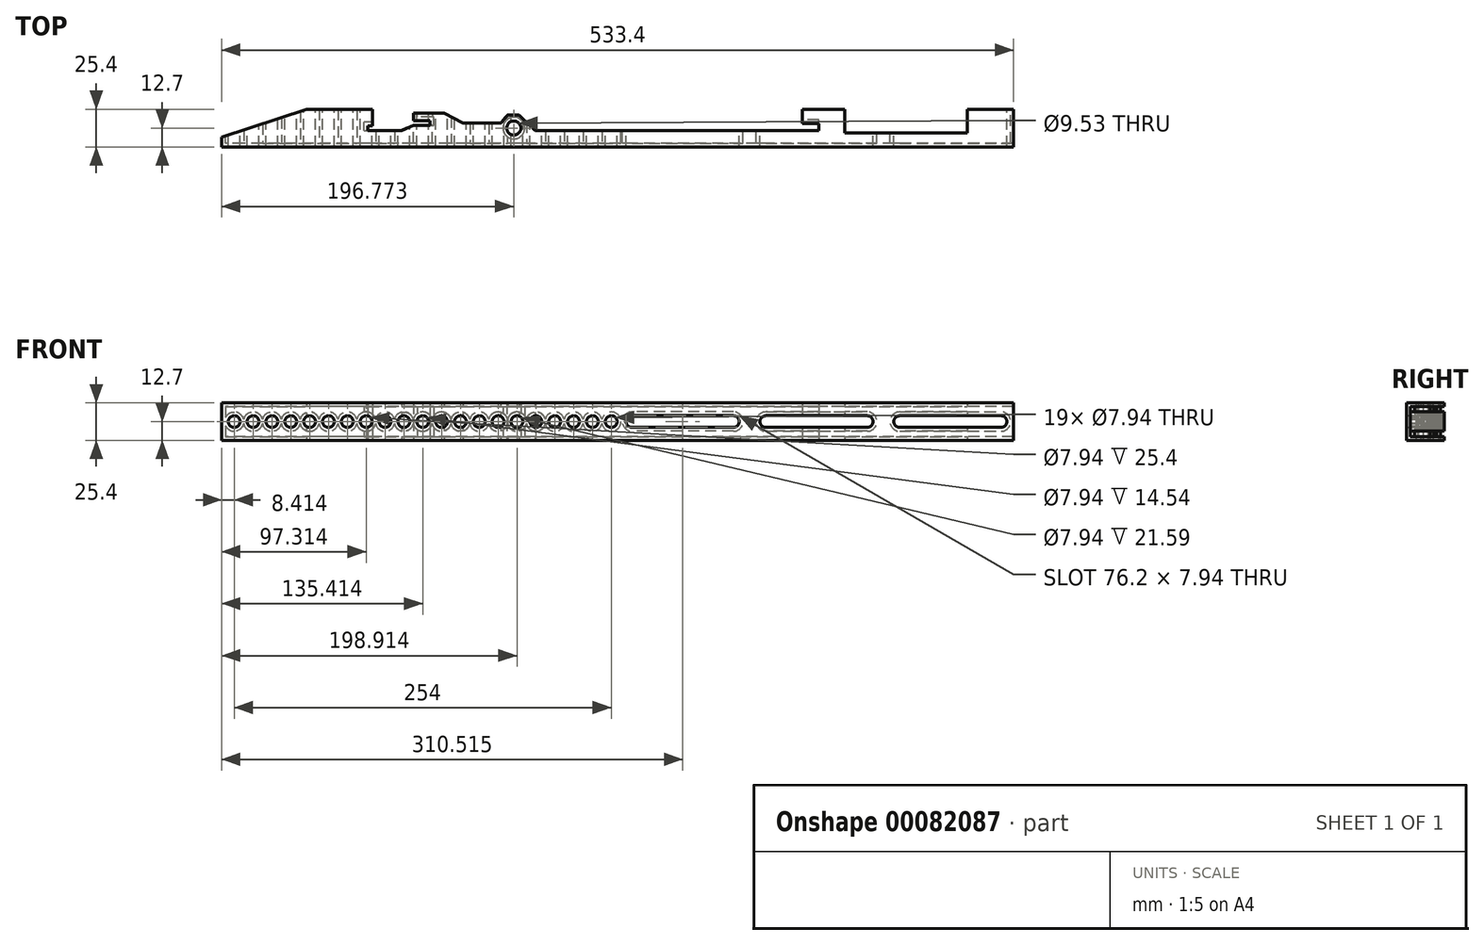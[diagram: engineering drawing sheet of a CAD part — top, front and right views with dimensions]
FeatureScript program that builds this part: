
annotation { "Feature Type Name" : "Feature", "Feature Type Description" : "" }
export const myFeature = defineFeature(function(context is Context, id is Id, definition is map)
    precondition{}
    {
        {
            var Q0;
            Q0=qCreatedBy(makeId("Front.planeOp"),FACE);
            var sketch = newSketch(context, id + "F0", { "sketchPlane" : qUnion([Q0])});
            skLineSegment(sketch, "E0.bottom", {"start": v(0, 0) * mm, "end": v(-533.4, 0) * mm});
            skLineSegment(sketch, "E0.top", {"start": v(0, 25.4) * mm, "end": v(-533.4, 25.4) * mm});
            skLineSegment(sketch, "E0.left", {"start": v(0, 0) * mm, "end": v(0, 25.4) * mm});
            skLineSegment(sketch, "E0.right", {"start": v(-533.4, 0) * mm, "end": v(-533.4, 25.4) * mm});
            skLineSegment(sketch, "E1", {"start": v(-266.7, 25.4) * mm, "end": v(-266.7, 0) * mm, "construction": true});
            skLineSegment(sketch, "E2", {"start": v(0, 12.7) * mm, "end": v(-533.4, 12.7) * mm, "construction": true});
            skCircle(sketch, "E3", {"center": v(-524.99, 12.7) * mm, "radius": 3.97 * mm});
            skCircle(sketch, "E4.1.0.0", {"center": v(-512.29, 12.7) * mm, "radius": 3.97 * mm});
            skCircle(sketch, "E4.2.0.0", {"center": v(-499.59, 12.7) * mm, "radius": 3.97 * mm});
            skCircle(sketch, "E4.3.0.0", {"center": v(-486.89, 12.7) * mm, "radius": 3.97 * mm});
            skCircle(sketch, "E4.4.0.0", {"center": v(-474.19, 12.7) * mm, "radius": 3.97 * mm});
            skCircle(sketch, "E4.5.0.0", {"center": v(-461.49, 12.7) * mm, "radius": 3.97 * mm});
            skCircle(sketch, "E4.6.0.0", {"center": v(-448.79, 12.7) * mm, "radius": 3.97 * mm});
            skCircle(sketch, "E4.7.0.0", {"center": v(-436.09, 12.7) * mm, "radius": 3.97 * mm});
            skCircle(sketch, "E4.8.0.0", {"center": v(-423.39, 12.7) * mm, "radius": 3.97 * mm});
            skCircle(sketch, "E4.9.0.0", {"center": v(-410.69, 12.7) * mm, "radius": 3.97 * mm});
            skCircle(sketch, "E4.10.0.0", {"center": v(-397.99, 12.7) * mm, "radius": 3.97 * mm});
            skCircle(sketch, "E4.11.0.0", {"center": v(-385.29, 12.7) * mm, "radius": 3.97 * mm});
            skCircle(sketch, "E4.12.0.0", {"center": v(-372.59, 12.7) * mm, "radius": 3.97 * mm});
            skCircle(sketch, "E4.13.0.0", {"center": v(-359.89, 12.7) * mm, "radius": 3.97 * mm});
            skCircle(sketch, "E4.14.0.0", {"center": v(-347.19, 12.7) * mm, "radius": 3.97 * mm});
            skCircle(sketch, "E4.15.0.0", {"center": v(-334.49, 12.7) * mm, "radius": 3.97 * mm});
            skCircle(sketch, "E4.16.0.0", {"center": v(-321.79, 12.7) * mm, "radius": 3.97 * mm});
            skCircle(sketch, "E4.17.0.0", {"center": v(-309.09, 12.7) * mm, "radius": 3.97 * mm});
            skCircle(sketch, "E4.18.0.0", {"center": v(-296.39, 12.7) * mm, "radius": 3.97 * mm});
            skCircle(sketch, "E4.19.0.0", {"center": v(-283.69, 12.7) * mm, "radius": 3.97 * mm});
            skCircle(sketch, "E4.20.0.0", {"center": v(-270.99, 12.7) * mm, "radius": 3.97 * mm});
            skLineSegment(sketch, "E4.direction1", {"start": v(-524.99, 12.7) * mm, "end": v(-512.29, 12.7) * mm, "construction": true});
            skCircle(sketch, "E5", {"center": v(-8.41, 12.7) * mm, "radius": 3.97 * mm});
            skCircle(sketch, "E6", {"center": v(-76.68, 12.7) * mm, "radius": 3.97 * mm});
            skLineSegment(sketch, "E7", {"start": v(-76.68, 16.67) * mm, "end": v(-8.41, 16.67) * mm});
            skLineSegment(sketch, "E8", {"start": v(-76.68, 8.73) * mm, "end": v(-8.41, 8.73) * mm});
            skCircle(sketch, "E9.1.0.0", {"center": v(-98.58, 12.7) * mm, "radius": 3.97 * mm});
            skLineSegment(sketch, "E9.1.0.1", {"start": v(-166.85, 8.73) * mm, "end": v(-98.58, 8.73) * mm});
            skLineSegment(sketch, "E9.1.0.2", {"start": v(-166.85, 16.67) * mm, "end": v(-98.58, 16.67) * mm});
            skCircle(sketch, "E9.1.0.3", {"center": v(-166.85, 12.7) * mm, "radius": 3.97 * mm});
            skCircle(sketch, "E9.2.0.0", {"center": v(-188.75, 12.7) * mm, "radius": 3.97 * mm});
            skLineSegment(sketch, "E9.2.0.1", {"start": v(-257.02, 8.73) * mm, "end": v(-188.75, 8.73) * mm});
            skLineSegment(sketch, "E9.2.0.2", {"start": v(-257.02, 16.67) * mm, "end": v(-188.75, 16.67) * mm});
            skCircle(sketch, "E9.2.0.3", {"center": v(-257.02, 12.7) * mm, "radius": 3.97 * mm});
            skLineSegment(sketch, "E9.direction1", {"start": v(-8.41, 12.7) * mm, "end": v(-98.58, 12.7) * mm, "construction": true});
            skSolve(sketch);
        }
        {
            var Q0;
            Q0=makeQuery(id+"F0.imprint","IMPRINT",FACE,{"disambiguationData":[TD([[makeQuery(id+"F0.imprint","IMPRINT",EDGE,{"derivedFrom":sQuery(id+"F0.wireOp",EDGE,"E0.bottom")}),-1.0]])]});
            extrude(context, id + "F1", {"entities" : qUnion([Q0]), "depth" : 25.4 * mm});
        }
        {
            var Q0;
            Q0=makeQuery(id+"F1.opExtrude","SWEPT_FACE",FACE,{"disambiguationData":[OSD([sQuery(id+"F0.wireOp",EDGE,"E0.bottom")])]});
            var sketch = newSketch(context, id + "F2", { "sketchPlane" : qUnion([Q0])});
            skLineSegment(sketch, "E10.0", {"start": v(0, 25.4) * mm, "end": v(-533.4, 25.4) * mm});
            skLineSegment(sketch, "E10.1", {"start": v(-533.4, 25.4) * mm, "end": v(-533.4, 0) * mm});
            skLineSegment(sketch, "E10.2", {"start": v(0, 0) * mm, "end": v(-533.4, 0) * mm});
            skLineSegment(sketch, "E10.3", {"start": v(0, 25.4) * mm, "end": v(0, 0) * mm});
            skLineSegment(sketch, "E11", {"start": v(-533.4, 18.84) * mm, "end": v(-476.25, 0) * mm});
            skLineSegment(sketch, "E12", {"start": v(-476.25, 0) * mm, "end": v(-431.8, 0) * mm});
            skLineSegment(sketch, "E13", {"start": v(-431.8, 0) * mm, "end": v(-431.8, 11.11) * mm});
            skLineSegment(sketch, "E14", {"start": v(-431.8, 11.11) * mm, "end": v(-434.98, 11.11) * mm});
            skLineSegment(sketch, "E15", {"start": v(-434.98, 11.11) * mm, "end": v(-434.98, 14.29) * mm});
            skLineSegment(sketch, "E16", {"start": v(-434.98, 14.29) * mm, "end": v(-412.11, 14.29) * mm});
            skLineSegment(sketch, "E17", {"start": v(-412.11, 14.29) * mm, "end": v(-404.17, 10.86) * mm});
            skLineSegment(sketch, "E18", {"start": v(-404.17, 10.86) * mm, "end": v(-393.06, 10.86) * mm});
            skLineSegment(sketch, "E19", {"start": v(-393.06, 10.86) * mm, "end": v(-393.06, 7.68) * mm});
            skLineSegment(sketch, "E20", {"start": v(-393.06, 7.68) * mm, "end": v(-404.17, 7.68) * mm});
            skLineSegment(sketch, "E21", {"start": v(-404.17, 7.68) * mm, "end": v(-404.17, 2.55) * mm});
            skLineSegment(sketch, "E22", {"start": v(-404.17, 2.55) * mm, "end": v(-383.54, 2.55) * mm});
            skLineSegment(sketch, "E23", {"start": v(-383.54, 2.55) * mm, "end": v(-370.84, 9.38) * mm});
            skLineSegment(sketch, "E24", {"start": v(-370.84, 9.38) * mm, "end": v(-345.44, 9.38) * mm});
            skLineSegment(sketch, "E25", {"start": v(-345.44, 9.38) * mm, "end": v(-340.79, 3.8) * mm});
            skLineSegment(sketch, "E26", {"start": v(-340.79, 3.8) * mm, "end": v(-333, 3.8) * mm});
            skLineSegment(sketch, "E27", {"start": v(-333, 3.8) * mm, "end": v(-322.3, 14.29) * mm});
            skLineSegment(sketch, "E28", {"start": v(-322.3, 14.29) * mm, "end": v(-131.13, 14.29) * mm});
            skLineSegment(sketch, "E29", {"start": v(-131.13, 14.29) * mm, "end": v(-131.13, 9.52) * mm});
            skLineSegment(sketch, "E30", {"start": v(-131.13, 9.52) * mm, "end": v(-142.24, 9.52) * mm});
            skLineSegment(sketch, "E31", {"start": v(-142.24, 9.52) * mm, "end": v(-142.24, 0) * mm});
            skLineSegment(sketch, "E32", {"start": v(-142.24, 0) * mm, "end": v(-113.67, 0) * mm});
            skLineSegment(sketch, "E33", {"start": v(-113.67, 0) * mm, "end": v(-113.67, 15.87) * mm});
            skLineSegment(sketch, "E34", {"start": v(-113.67, 15.87) * mm, "end": v(-31.12, 15.88) * mm});
            skLineSegment(sketch, "E35", {"start": v(-31.12, 15.88) * mm, "end": v(-31.12, 0) * mm});
            skLineSegment(sketch, "E36", {"start": v(-533.4, 12.7) * mm, "end": v(0, 12.7) * mm, "construction": true});
            skCircle(sketch, "E37", {"center": v(-336.63, 12.7) * mm, "radius": 4.76 * mm});
            skSolve(sketch);
        }
        {
            var Q0;
            {var subQ0=sQuery(id+"F2.wireOp",EDGE,"E13");Q0=makeQuery(id+"F2.imprint","IMPRINT",FACE,{"disambiguationData":[TD([[makeQuery(id+"F2.imprint","IMPRINT",EDGE,{"derivedFrom":subQ0}),-1.0]])]});}
            var Q1;
            Q1=makeQuery(id+"F2.imprint","IMPRINT",FACE,{"disambiguationData":[TD([[makeQuery(id+"F2.imprint","IMPRINT",EDGE,{"derivedFrom":sQuery(id+"F2.wireOp",EDGE,"E37")}),1.0]])]});
            var Q2;
            {var subQ3=sQuery(id+"F2.wireOp",EDGE,"E11");Q2=makeQuery(id+"F2.imprint","IMPRINT",FACE,{"disambiguationData":[TD([[makeQuery(id+"F2.imprint","IMPRINT",EDGE,{"derivedFrom":subQ3}),-1.0]])]});}
            var Q3;
            {var subQ0=sQuery(id+"F2.wireOp",EDGE,"E33");Q3=makeQuery(id+"F2.imprint","IMPRINT",FACE,{"disambiguationData":[TD([[makeQuery(id+"F2.imprint","IMPRINT",EDGE,{"derivedFrom":subQ0}),-1.0]])]});}
            extrude(context, id + "F3", {"entities" : qUnion([Q0, Q1, Q2, Q3]), "operationType" : NewBodyOperationType.REMOVE, "endBound" : BoundingType.THROUGH_ALL, "oppositeDirection" : true, "depth" : 25.4 * mm});
        }
        {
            var Q0;
            Q0=makeQuery(id+"F3.boolean.opBoolean","COPY",FACE,{"derivedFrom":makeQuery(id+"F3.opExtrude","SWEPT_FACE",FACE,{"disambiguationData":[OSD([sQuery(id+"F2.wireOp",EDGE,"E11")])]})});
            var Q1;
            {var subQ0=sQuery(id+"F0.wireOp",EDGE,"E4.5.0.0");var subQ1=sQuery(id+"F0.wireOp",EDGE,"E4.4.0.0");var subQ2=sQuery(id+"F0.wireOp",EDGE,"E0.top");var subQ3=sQuery(id+"F0.wireOp",EDGE,"E0.bottom");var subQ4=sQuery(id+"F0.wireOp",EDGE,"E4.6.0.0");var subQ5=sQuery(id+"F0.wireOp",EDGE,"E4.7.0.0");Q1=makeQuery(id+"F3.boolean.opBoolean","SPLIT",FACE,{"disambiguationData":[TD([makeQuery(id+"F1.opExtrude","SWEPT_FACE",FACE,{"disambiguationData":[OSD([subQ1])]})])],"derivedFrom":makeQuery(id+"F1.opExtrude","CAP_FACE",FACE,{"disambiguationData":[OSD([subQ3,subQ2,sQuery(id+"F0.wireOp",EDGE,"E0.left"),sQuery(id+"F0.wireOp",EDGE,"E0.right"),sQuery(id+"F0.wireOp",EDGE,"E3"),sQuery(id+"F0.wireOp",EDGE,"E4.1.0.0"),sQuery(id+"F0.wireOp",EDGE,"E4.2.0.0"),sQuery(id+"F0.wireOp",EDGE,"E4.3.0.0"),subQ1,subQ0,subQ4,subQ5,sQuery(id+"F0.wireOp",EDGE,"E4.8.0.0"),sQuery(id+"F0.wireOp",EDGE,"E4.9.0.0"),sQuery(id+"F0.wireOp",EDGE,"E4.10.0.0"),sQuery(id+"F0.wireOp",EDGE,"E4.11.0.0"),sQuery(id+"F0.wireOp",EDGE,"E4.12.0.0"),sQuery(id+"F0.wireOp",EDGE,"E4.13.0.0"),sQuery(id+"F0.wireOp",EDGE,"E4.14.0.0"),sQuery(id+"F0.wireOp",EDGE,"E4.15.0.0"),sQuery(id+"F0.wireOp",EDGE,"E4.16.0.0"),sQuery(id+"F0.wireOp",EDGE,"E4.17.0.0"),sQuery(id+"F0.wireOp",EDGE,"E4.18.0.0"),sQuery(id+"F0.wireOp",EDGE,"E4.19.0.0"),sQuery(id+"F0.wireOp",EDGE,"E4.20.0.0"),sQuery(id+"F0.wireOp",EDGE,"E5"),sQuery(id+"F0.wireOp",EDGE,"E6"),sQuery(id+"F0.wireOp",EDGE,"E7"),sQuery(id+"F0.wireOp",EDGE,"E8"),sQuery(id+"F0.wireOp",EDGE,"E9.1.0.0"),sQuery(id+"F0.wireOp",EDGE,"E9.1.0.1"),sQuery(id+"F0.wireOp",EDGE,"E9.1.0.2"),sQuery(id+"F0.wireOp",EDGE,"E9.1.0.3"),sQuery(id+"F0.wireOp",EDGE,"E9.2.0.0"),sQuery(id+"F0.wireOp",EDGE,"E9.2.0.1"),sQuery(id+"F0.wireOp",EDGE,"E9.2.0.2"),sQuery(id+"F0.wireOp",EDGE,"E9.2.0.3")])],"isStart":true})});}
            var Q2;
            Q2=makeQuery(id+"F3.boolean.opBoolean","COPY",FACE,{"derivedFrom":makeQuery(id+"F3.opExtrude","SWEPT_FACE",FACE,{"disambiguationData":[OSD([sQuery(id+"F2.wireOp",EDGE,"E16")])]})});
            var Q3;
            Q3=makeQuery(id+"F3.boolean.opBoolean","COPY",FACE,{"derivedFrom":makeQuery(id+"F3.opExtrude","SWEPT_FACE",FACE,{"disambiguationData":[OSD([sQuery(id+"F2.wireOp",EDGE,"E17")])]})});
            var Q4;
            Q4=makeQuery(id+"F3.boolean.opBoolean","COPY",FACE,{"derivedFrom":makeQuery(id+"F3.opExtrude","SWEPT_FACE",FACE,{"disambiguationData":[OSD([sQuery(id+"F2.wireOp",EDGE,"E22")])]})});
            var Q5;
            Q5=makeQuery(id+"F3.boolean.opBoolean","COPY",FACE,{"derivedFrom":makeQuery(id+"F3.opExtrude","SWEPT_FACE",FACE,{"disambiguationData":[OSD([sQuery(id+"F2.wireOp",EDGE,"E23")])]})});
            var Q6;
            Q6=makeQuery(id+"F3.boolean.opBoolean","COPY",FACE,{"derivedFrom":makeQuery(id+"F3.opExtrude","SWEPT_FACE",FACE,{"disambiguationData":[OSD([sQuery(id+"F2.wireOp",EDGE,"E24")])]})});
            var Q7;
            Q7=makeQuery(id+"F3.boolean.opBoolean","COPY",FACE,{"derivedFrom":makeQuery(id+"F3.opExtrude","SWEPT_FACE",FACE,{"disambiguationData":[OSD([sQuery(id+"F2.wireOp",EDGE,"E26")])]})});
            var Q8;
            Q8=makeQuery(id+"F3.boolean.opBoolean","COPY",FACE,{"derivedFrom":makeQuery(id+"F3.opExtrude","SWEPT_FACE",FACE,{"disambiguationData":[OSD([sQuery(id+"F2.wireOp",EDGE,"E27")])]})});
            var Q9;
            Q9=makeQuery(id+"F3.boolean.opBoolean","COPY",FACE,{"derivedFrom":makeQuery(id+"F3.opExtrude","SWEPT_FACE",FACE,{"disambiguationData":[OSD([sQuery(id+"F2.wireOp",EDGE,"E28")])]})});
            var Q10;
            Q10=makeQuery(id+"F3.boolean.opBoolean","COPY",FACE,{"derivedFrom":makeQuery(id+"F3.opExtrude","SWEPT_FACE",FACE,{"disambiguationData":[OSD([sQuery(id+"F2.wireOp",EDGE,"E34")])]})});
            var Q11;
            {var subQ0=sQuery(id+"F0.wireOp",EDGE,"E0.bottom");var subQ1=sQuery(id+"F0.wireOp",EDGE,"E9.1.0.1");Q11=makeQuery(id+"F3.boolean.opBoolean","SPLIT",FACE,{"disambiguationData":[TD([makeQuery(id+"F1.opExtrude","SWEPT_FACE",FACE,{"disambiguationData":[OSD([subQ1])]})])],"derivedFrom":makeQuery(id+"F1.opExtrude","CAP_FACE",FACE,{"disambiguationData":[OSD([subQ0,sQuery(id+"F0.wireOp",EDGE,"E0.top"),sQuery(id+"F0.wireOp",EDGE,"E0.left"),sQuery(id+"F0.wireOp",EDGE,"E0.right"),sQuery(id+"F0.wireOp",EDGE,"E3"),sQuery(id+"F0.wireOp",EDGE,"E4.1.0.0"),sQuery(id+"F0.wireOp",EDGE,"E4.2.0.0"),sQuery(id+"F0.wireOp",EDGE,"E4.3.0.0"),sQuery(id+"F0.wireOp",EDGE,"E4.4.0.0"),sQuery(id+"F0.wireOp",EDGE,"E4.5.0.0"),sQuery(id+"F0.wireOp",EDGE,"E4.6.0.0"),sQuery(id+"F0.wireOp",EDGE,"E4.7.0.0"),sQuery(id+"F0.wireOp",EDGE,"E4.8.0.0"),sQuery(id+"F0.wireOp",EDGE,"E4.9.0.0"),sQuery(id+"F0.wireOp",EDGE,"E4.10.0.0"),sQuery(id+"F0.wireOp",EDGE,"E4.11.0.0"),sQuery(id+"F0.wireOp",EDGE,"E4.12.0.0"),sQuery(id+"F0.wireOp",EDGE,"E4.13.0.0"),sQuery(id+"F0.wireOp",EDGE,"E4.14.0.0"),sQuery(id+"F0.wireOp",EDGE,"E4.15.0.0"),sQuery(id+"F0.wireOp",EDGE,"E4.16.0.0"),sQuery(id+"F0.wireOp",EDGE,"E4.17.0.0"),sQuery(id+"F0.wireOp",EDGE,"E4.18.0.0"),sQuery(id+"F0.wireOp",EDGE,"E4.19.0.0"),sQuery(id+"F0.wireOp",EDGE,"E4.20.0.0"),sQuery(id+"F0.wireOp",EDGE,"E5"),sQuery(id+"F0.wireOp",EDGE,"E6"),sQuery(id+"F0.wireOp",EDGE,"E7"),sQuery(id+"F0.wireOp",EDGE,"E8"),sQuery(id+"F0.wireOp",EDGE,"E9.1.0.0"),subQ1,sQuery(id+"F0.wireOp",EDGE,"E9.1.0.2"),sQuery(id+"F0.wireOp",EDGE,"E9.1.0.3"),sQuery(id+"F0.wireOp",EDGE,"E9.2.0.0"),sQuery(id+"F0.wireOp",EDGE,"E9.2.0.1"),sQuery(id+"F0.wireOp",EDGE,"E9.2.0.2"),sQuery(id+"F0.wireOp",EDGE,"E9.2.0.3")])],"isStart":true})});}
            var Q12;
            {var subQ0=sQuery(id+"F0.wireOp",EDGE,"E0.top");var subQ1=sQuery(id+"F0.wireOp",EDGE,"E9.1.0.2");Q12=makeQuery(id+"F3.boolean.opBoolean","SPLIT",FACE,{"disambiguationData":[TD([makeQuery(id+"F1.opExtrude","SWEPT_FACE",FACE,{"disambiguationData":[OSD([subQ1])]})])],"derivedFrom":makeQuery(id+"F1.opExtrude","CAP_FACE",FACE,{"disambiguationData":[OSD([sQuery(id+"F0.wireOp",EDGE,"E0.bottom"),subQ0,sQuery(id+"F0.wireOp",EDGE,"E0.left"),sQuery(id+"F0.wireOp",EDGE,"E0.right"),sQuery(id+"F0.wireOp",EDGE,"E3"),sQuery(id+"F0.wireOp",EDGE,"E4.1.0.0"),sQuery(id+"F0.wireOp",EDGE,"E4.2.0.0"),sQuery(id+"F0.wireOp",EDGE,"E4.3.0.0"),sQuery(id+"F0.wireOp",EDGE,"E4.4.0.0"),sQuery(id+"F0.wireOp",EDGE,"E4.5.0.0"),sQuery(id+"F0.wireOp",EDGE,"E4.6.0.0"),sQuery(id+"F0.wireOp",EDGE,"E4.7.0.0"),sQuery(id+"F0.wireOp",EDGE,"E4.8.0.0"),sQuery(id+"F0.wireOp",EDGE,"E4.9.0.0"),sQuery(id+"F0.wireOp",EDGE,"E4.10.0.0"),sQuery(id+"F0.wireOp",EDGE,"E4.11.0.0"),sQuery(id+"F0.wireOp",EDGE,"E4.12.0.0"),sQuery(id+"F0.wireOp",EDGE,"E4.13.0.0"),sQuery(id+"F0.wireOp",EDGE,"E4.14.0.0"),sQuery(id+"F0.wireOp",EDGE,"E4.15.0.0"),sQuery(id+"F0.wireOp",EDGE,"E4.16.0.0"),sQuery(id+"F0.wireOp",EDGE,"E4.17.0.0"),sQuery(id+"F0.wireOp",EDGE,"E4.18.0.0"),sQuery(id+"F0.wireOp",EDGE,"E4.19.0.0"),sQuery(id+"F0.wireOp",EDGE,"E4.20.0.0"),sQuery(id+"F0.wireOp",EDGE,"E5"),sQuery(id+"F0.wireOp",EDGE,"E6"),sQuery(id+"F0.wireOp",EDGE,"E7"),sQuery(id+"F0.wireOp",EDGE,"E8"),sQuery(id+"F0.wireOp",EDGE,"E9.1.0.0"),sQuery(id+"F0.wireOp",EDGE,"E9.1.0.1"),subQ1,sQuery(id+"F0.wireOp",EDGE,"E9.1.0.3"),sQuery(id+"F0.wireOp",EDGE,"E9.2.0.0"),sQuery(id+"F0.wireOp",EDGE,"E9.2.0.1"),sQuery(id+"F0.wireOp",EDGE,"E9.2.0.2"),sQuery(id+"F0.wireOp",EDGE,"E9.2.0.3")])],"isStart":true})});}
            var Q13;
            Q13=makeQuery(id+"F3.boolean.opBoolean","COPY",FACE,{"derivedFrom":makeQuery(id+"F3.opExtrude","SWEPT_FACE",FACE,{"disambiguationData":[OSD([sQuery(id+"F2.wireOp",EDGE,"E13")])]})});
            var Q14;
            Q14=makeQuery(id+"F3.boolean.opBoolean","COPY",FACE,{"derivedFrom":makeQuery(id+"F3.opExtrude","SWEPT_FACE",FACE,{"disambiguationData":[OSD([sQuery(id+"F2.wireOp",EDGE,"E18")])]})});
            var Q15;
            Q15=makeQuery(id+"F3.boolean.opBoolean","COPY",FACE,{"derivedFrom":makeQuery(id+"F3.opExtrude","SWEPT_FACE",FACE,{"disambiguationData":[OSD([sQuery(id+"F2.wireOp",EDGE,"E25")])]})});
            var Q16;
            Q16=makeQuery(id+"F3.boolean.opBoolean","COPY",FACE,{"disambiguationData":[OD(0.0)],"derivedFrom":makeQuery(id+"F3.opExtrude","SWEPT_FACE",FACE,{"disambiguationData":[OSD([sQuery(id+"F2.wireOp",EDGE,"E35")])]})});
            var Q17;
            Q17=makeQuery(id+"F3.boolean.opBoolean","COPY",FACE,{"disambiguationData":[OD(1.0)],"derivedFrom":makeQuery(id+"F3.opExtrude","SWEPT_FACE",FACE,{"disambiguationData":[OSD([sQuery(id+"F2.wireOp",EDGE,"E35")])]})});
            var Q18;
            {var subQ0=sQuery(id+"F0.wireOp",EDGE,"E0.left");var subQ1=sQuery(id+"F0.wireOp",EDGE,"E5");var subQ2=sQuery(id+"F0.wireOp",EDGE,"E8");var subQ3=sQuery(id+"F0.wireOp",EDGE,"E0.top");var subQ4=sQuery(id+"F0.wireOp",EDGE,"E7");var subQ5=sQuery(id+"F0.wireOp",EDGE,"E0.bottom");Q18=makeQuery(id+"F3.boolean.opBoolean","SPLIT",FACE,{"disambiguationData":[TD([makeQuery(id+"F1.opExtrude","SWEPT_FACE",FACE,{"disambiguationData":[OSD([subQ0])]})])],"derivedFrom":makeQuery(id+"F1.opExtrude","CAP_FACE",FACE,{"disambiguationData":[OSD([subQ5,subQ3,subQ0,sQuery(id+"F0.wireOp",EDGE,"E0.right"),sQuery(id+"F0.wireOp",EDGE,"E3"),sQuery(id+"F0.wireOp",EDGE,"E4.1.0.0"),sQuery(id+"F0.wireOp",EDGE,"E4.2.0.0"),sQuery(id+"F0.wireOp",EDGE,"E4.3.0.0"),sQuery(id+"F0.wireOp",EDGE,"E4.4.0.0"),sQuery(id+"F0.wireOp",EDGE,"E4.5.0.0"),sQuery(id+"F0.wireOp",EDGE,"E4.6.0.0"),sQuery(id+"F0.wireOp",EDGE,"E4.7.0.0"),sQuery(id+"F0.wireOp",EDGE,"E4.8.0.0"),sQuery(id+"F0.wireOp",EDGE,"E4.9.0.0"),sQuery(id+"F0.wireOp",EDGE,"E4.10.0.0"),sQuery(id+"F0.wireOp",EDGE,"E4.11.0.0"),sQuery(id+"F0.wireOp",EDGE,"E4.12.0.0"),sQuery(id+"F0.wireOp",EDGE,"E4.13.0.0"),sQuery(id+"F0.wireOp",EDGE,"E4.14.0.0"),sQuery(id+"F0.wireOp",EDGE,"E4.15.0.0"),sQuery(id+"F0.wireOp",EDGE,"E4.16.0.0"),sQuery(id+"F0.wireOp",EDGE,"E4.17.0.0"),sQuery(id+"F0.wireOp",EDGE,"E4.18.0.0"),sQuery(id+"F0.wireOp",EDGE,"E4.19.0.0"),sQuery(id+"F0.wireOp",EDGE,"E4.20.0.0"),subQ1,sQuery(id+"F0.wireOp",EDGE,"E6"),subQ4,subQ2,sQuery(id+"F0.wireOp",EDGE,"E9.1.0.0"),sQuery(id+"F0.wireOp",EDGE,"E9.1.0.1"),sQuery(id+"F0.wireOp",EDGE,"E9.1.0.2"),sQuery(id+"F0.wireOp",EDGE,"E9.1.0.3"),sQuery(id+"F0.wireOp",EDGE,"E9.2.0.0"),sQuery(id+"F0.wireOp",EDGE,"E9.2.0.1"),sQuery(id+"F0.wireOp",EDGE,"E9.2.0.2"),sQuery(id+"F0.wireOp",EDGE,"E9.2.0.3")])],"isStart":true})});}
            var Q19;
            Q19=makeQuery(id+"F3.boolean.opBoolean","COPY",FACE,{"disambiguationData":[OD(0.0)],"derivedFrom":makeQuery(id+"F3.opExtrude","SWEPT_FACE",FACE,{"disambiguationData":[OSD([sQuery(id+"F2.wireOp",EDGE,"E31")])]})});
            var Q20;
            Q20=makeQuery(id+"F3.boolean.opBoolean","COPY",FACE,{"disambiguationData":[OD(1.0)],"derivedFrom":makeQuery(id+"F3.opExtrude","SWEPT_FACE",FACE,{"disambiguationData":[OSD([sQuery(id+"F2.wireOp",EDGE,"E31")])]})});
            var Q21;
            Q21=makeQuery(id+"F3.boolean.opBoolean","COPY",FACE,{"disambiguationData":[OD(1.0)],"derivedFrom":makeQuery(id+"F3.opExtrude","SWEPT_FACE",FACE,{"disambiguationData":[OSD([sQuery(id+"F2.wireOp",EDGE,"E29")])]})});
            var Q22;
            Q22=makeQuery(id+"F3.boolean.opBoolean","COPY",FACE,{"disambiguationData":[OD(0.0)],"derivedFrom":makeQuery(id+"F3.opExtrude","SWEPT_FACE",FACE,{"disambiguationData":[OSD([sQuery(id+"F2.wireOp",EDGE,"E29")])]})});
            var Q23;
            Q23=makeQuery(id+"F1.opExtrude","SWEPT_FACE",FACE,{"disambiguationData":[OSD([sQuery(id+"F0.wireOp",EDGE,"E0.left")])]});
            var Q24;
            Q24=makeQuery(id+"F3.boolean.opBoolean","COPY",FACE,{"disambiguationData":[OD(0.0)],"derivedFrom":makeQuery(id+"F3.opExtrude","SWEPT_FACE",FACE,{"disambiguationData":[OSD([sQuery(id+"F2.wireOp",EDGE,"E33")])]})});
            var Q25;
            Q25=makeQuery(id+"F3.boolean.opBoolean","COPY",FACE,{"disambiguationData":[OD(1.0)],"derivedFrom":makeQuery(id+"F3.opExtrude","SWEPT_FACE",FACE,{"disambiguationData":[OSD([sQuery(id+"F2.wireOp",EDGE,"E33")])]})});
            shell(context, id + "F4", {"entities" : qUnion([Q0, Q1, Q2, Q3, Q4, Q5, Q6, Q7, Q8, Q9, Q10, Q11, Q12, Q13, Q14, Q15, Q16, Q17, Q18, Q19, Q20, Q21, Q22, Q23, Q24, Q25]), "thickness" : 2.54 * mm});
        }
    });
